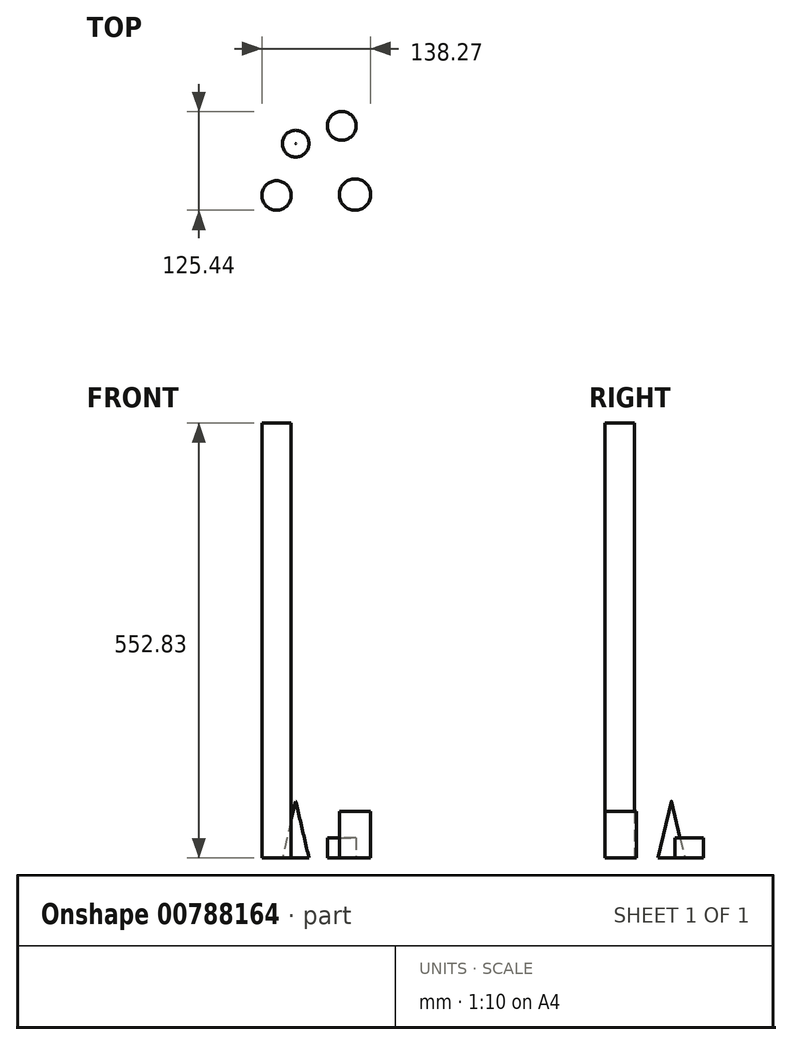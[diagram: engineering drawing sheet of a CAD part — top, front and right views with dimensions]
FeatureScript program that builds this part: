
annotation { "Feature Type Name" : "Feature", "Feature Type Description" : "" }
export const myFeature = defineFeature(function(context is Context, id is Id, definition is map)
    precondition{}
    {
        {
            var Q0;
            Q0=qCreatedBy(makeId("Top.planeOp"),FACE);
            var sketch = newSketch(context, id + "F0", { "sketchPlane" : qUnion([Q0])});
            skCircle(sketch, "E0", {"center": v(52.66, -46.17) * mm, "radius": 19.97 * mm});
            skSolve(sketch);
        }
        {
            var Q0;
            Q0=makeQuery(id+"F0.imprint","IMPRINT",FACE,{"disambiguationData":[TD([[makeQuery(id+"F0.imprint","IMPRINT",EDGE,{"derivedFrom":sQuery(id+"F0.wireOp",EDGE,"E0")}),1.0]])]});
            extrude(context, id + "F1", {"entities" : qUnion([Q0]), "depth" : 59.02 * mm, "offsetDistance" : 25.4 * mm});
        }
        {
            var Q0;
            Q0=qCreatedBy(makeId("Top.planeOp"),FACE);
            var sketch = newSketch(context, id + "F2", { "sketchPlane" : qUnion([Q0])});
            skCircle(sketch, "E1", {"center": v(35.79, 41.06) * mm, "radius": 18.24 * mm});
            skSolve(sketch);
        }
        {
            var Q0;
            Q0=makeQuery(id+"F2.imprint","IMPRINT",FACE,{"disambiguationData":[TD([[makeQuery(id+"F2.imprint","IMPRINT",EDGE,{"derivedFrom":sQuery(id+"F2.wireOp",EDGE,"E1")}),1.0]])]});
            extrude(context, id + "F3", {"entities" : qUnion([Q0]), "depth" : 25.4 * mm, "offsetDistance" : 25.4 * mm});
        }
        {
            var Q0;
            Q0=qCreatedBy(makeId("Top.planeOp"),FACE);
            var sketch = newSketch(context, id + "F4", { "sketchPlane" : qUnion([Q0])});
            skCircle(sketch, "E2", {"center": v(-53.31, 54.35) * mm, "radius": 21.41 * mm});
            skSolve(sketch);
        }
        {
            var Q0;
            Q0=sQuery(id+"F4.wireOp",EDGE,"E2");
            extrude(context, id + "F5", {"bodyType" : ToolBodyType.SURFACE, "surfaceEntities" : qUnion([Q0]), "depth" : 494.85 * mm, "offsetDistance" : 25.4 * mm});
        }
        {
            var Q0;
            Q0=qCreatedBy(makeId("Top.planeOp"),FACE);
            var sketch = newSketch(context, id + "F6", { "sketchPlane" : qUnion([Q0])});
            skCircle(sketch, "E3", {"center": v(-46.97, -47.28) * mm, "radius": 18.66 * mm});
            skSolve(sketch);
        }
        {
            var Q0;
            Q0=makeQuery(id+"F6.imprint","IMPRINT",FACE,{"disambiguationData":[TD([[makeQuery(id+"F6.imprint","IMPRINT",EDGE,{"derivedFrom":sQuery(id+"F6.wireOp",EDGE,"E3")}),1.0]])]});
            extrude(context, id + "F7", {"entities" : qUnion([Q0]), "depth" : 552.83 * mm, "offsetDistance" : 25.4 * mm});
        }
        {
            var Q0;
            Q0=qCreatedBy(makeId("Top.planeOp"),FACE);
            var sketch = newSketch(context, id + "F8", { "sketchPlane" : qUnion([Q0])});
            skCircle(sketch, "E4", {"center": v(-22.72, 18.56) * mm, "radius": 17.88 * mm});
            skSolve(sketch);
        }
        {
            var Q0;
            Q0=makeQuery(id+"F8.imprint","IMPRINT",FACE,{"disambiguationData":[TD([[makeQuery(id+"F8.imprint","IMPRINT",EDGE,{"derivedFrom":sQuery(id+"F8.wireOp",EDGE,"E4")}),1.0]])]});
            extrude(context, id + "F9", {"entities" : qUnion([Q0]), "depth" : 72.15 * mm, "offsetDistance" : 25.4 * mm});
        }
        {
            var Q0;
            Q0=makeQuery(id+"F9.opExtrude","CAP_FACE",FACE,{"disambiguationData":[OSD([sQuery(id+"F8.wireOp",EDGE,"E4")])],"isStart":false});
            var Q1;
            Q1=makeQuery(id+"F9.opExtrude","CAP_EDGE",EDGE,{"disambiguationData":[OSD([sQuery(id+"F8.wireOp",EDGE,"E4")])],"isStart":false});
            chamfer(context, id + "F10", {"entities" : qUnion([Q0, Q1]), "chamferType" : ChamferType.TWO_OFFSETS, "width1" : 17.78 * mm, "oppositeDirection" : false, "width2" : 76.2 * mm});
        }
    });
